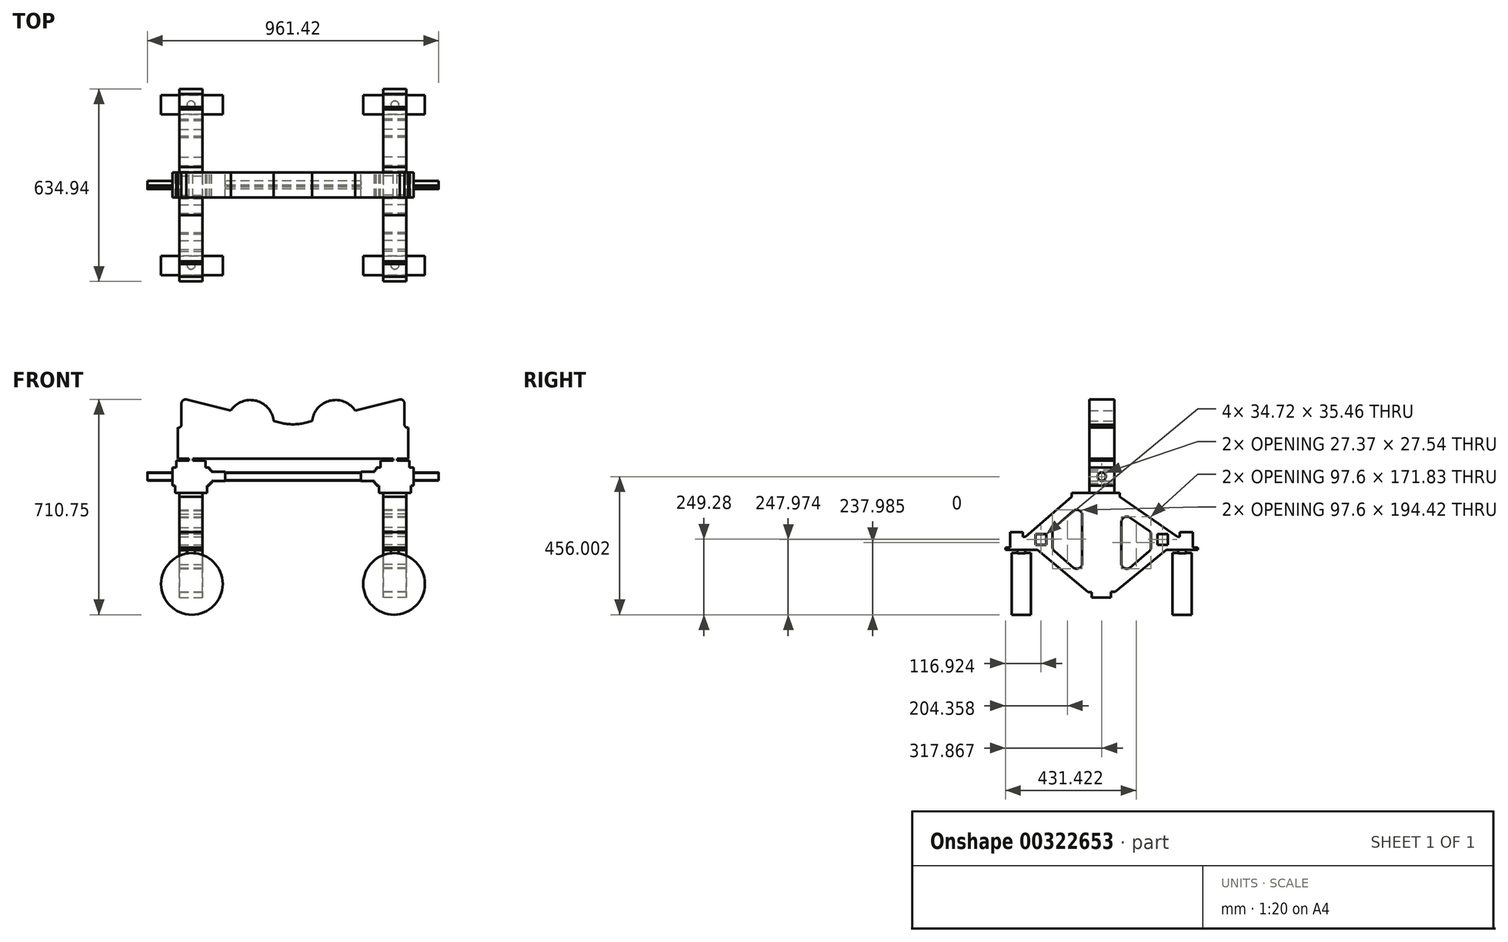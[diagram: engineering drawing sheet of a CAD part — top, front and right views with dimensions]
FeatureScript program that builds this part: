
annotation { "Feature Type Name" : "Feature", "Feature Type Description" : "" }
export const myFeature = defineFeature(function(context is Context, id is Id, definition is map)
    precondition{}
    {
        {
            var Q0;
            Q0=qCreatedBy(makeId("Front.planeOp"),FACE);
            var sketch = newSketch(context, id + "F0", { "sketchPlane" : qUnion([Q0])});
            skLineSegment(sketch, "E0", {"start": v(0, 0) * mm, "end": v(-380.7, 0) * mm});
            skLineSegment(sketch, "E1", {"start": v(-380.7, 0) * mm, "end": v(-380.7, 102.32) * mm});
            skArc(sketch, "E2", {"start": v(-380.7, 102.32) * mm, "mid": v(-372.54, 104.11) * mm, "end": v(-368.21, 111.26) * mm});
            skLineSegment(sketch, "E3", {"start": v(-368.21, 111.26) * mm, "end": v(-368.21, 182.25) * mm});
            skArc(sketch, "E4", {"start": v(-352.72, 195.3) * mm, "mid": v(-363.5, 192.37) * mm, "end": v(-368.21, 182.25) * mm});
            skLineSegment(sketch, "E5", {"start": v(-352.72, 195.3) * mm, "end": v(-38.9, 118.02) * mm});
            skLineSegment(sketch, "E6", {"start": v(0, 0) * mm, "end": v(0, 0) * mm});
            skArc(sketch, "E7.MirrorCS", {"start": v(380.7, 102.32) * mm, "mid": v(372.54, 104.11) * mm, "end": v(368.21, 111.26) * mm});
            skLineSegment(sketch, "E8.MirrorCS", {"start": v(368.21, 111.26) * mm, "end": v(368.21, 182.25) * mm});
            skArc(sketch, "E9.MirrorCS", {"start": v(352.72, 195.3) * mm, "mid": v(363.5, 192.37) * mm, "end": v(368.21, 182.25) * mm});
            skLineSegment(sketch, "E10.MirrorCS", {"start": v(0, 0) * mm, "end": v(380.7, 0) * mm});
            skLineSegment(sketch, "E11.MirrorCS", {"start": v(380.7, 0) * mm, "end": v(380.7, 102.32) * mm});
            skLineSegment(sketch, "E12.MirrorCS", {"start": v(352.72, 195.3) * mm, "end": v(38.9, 118.02) * mm});
            skArc(sketch, "E13", {"start": v(-38.9, 118.02) * mm, "mid": v(0, 113.3) * mm, "end": v(38.9, 118.02) * mm});
            skLineSegment(sketch, "E14", {"start": v(224.33, -43.67) * mm, "end": v(269.45, -43.67) * mm});
            skLineSegment(sketch, "E15", {"start": v(269.45, -43.67) * mm, "end": v(269.45, -36.61) * mm});
            skLineSegment(sketch, "E16", {"start": v(269.45, -36.61) * mm, "end": v(275.59, -36.61) * mm});
            skLineSegment(sketch, "E17", {"start": v(275.59, -36.61) * mm, "end": v(275.59, -29.55) * mm});
            skLineSegment(sketch, "E18", {"start": v(275.59, -29.55) * mm, "end": v(288.48, -29.55) * mm});
            skLineSegment(sketch, "E19", {"start": v(288.48, -29.55) * mm, "end": v(288.48, -5.92) * mm});
            skLineSegment(sketch, "E20", {"start": v(288.48, -5.92) * mm, "end": v(330.53, -5.92) * mm});
            skLineSegment(sketch, "E21", {"start": v(330.53, -5.92) * mm, "end": v(330.53, 0) * mm});
            skLineSegment(sketch, "E22", {"start": v(330.53, 0) * mm, "end": v(343.42, 0) * mm});
            skLineSegment(sketch, "E23", {"start": v(343.42, 0) * mm, "end": v(343.42, -5.92) * mm});
            skLineSegment(sketch, "E24", {"start": v(343.42, -5.92) * mm, "end": v(384.86, -5.92) * mm});
            skLineSegment(sketch, "E25", {"start": v(384.86, -5.92) * mm, "end": v(384.86, -29.55) * mm});
            skLineSegment(sketch, "E26", {"start": v(384.86, -29.55) * mm, "end": v(397.75, -29.55) * mm});
            skLineSegment(sketch, "E27", {"start": v(397.75, -29.55) * mm, "end": v(397.75, -88.49) * mm});
            skLineSegment(sketch, "E28", {"start": v(397.75, -88.49) * mm, "end": v(388.85, -88.49) * mm});
            skLineSegment(sketch, "E29", {"start": v(388.85, -88.49) * mm, "end": v(388.85, -112.74) * mm});
            skLineSegment(sketch, "E30", {"start": v(388.85, -112.74) * mm, "end": v(283.57, -112.74) * mm});
            skLineSegment(sketch, "E31", {"start": v(283.57, -112.74) * mm, "end": v(283.57, -88.49) * mm});
            skLineSegment(sketch, "E32", {"start": v(283.57, -88.49) * mm, "end": v(275.59, -88.49) * mm});
            skLineSegment(sketch, "E33", {"start": v(275.59, -88.49) * mm, "end": v(275.59, -80.81) * mm});
            skLineSegment(sketch, "E34", {"start": v(275.59, -80.81) * mm, "end": v(268.53, -80.81) * mm});
            skLineSegment(sketch, "E35", {"start": v(268.53, -80.81) * mm, "end": v(268.53, -73.14) * mm});
            skLineSegment(sketch, "E36", {"start": v(268.53, -73.14) * mm, "end": v(224.33, -73.14) * mm});
            skLineSegment(sketch, "E37", {"start": v(224.33, -73.14) * mm, "end": v(224.33, -43.67) * mm});
            skLineSegment(sketch, "E38", {"start": v(0, -43.67) * mm, "end": v(0, -73.14) * mm, "construction": true});
            skLineSegment(sketch, "E39.MirrorCS", {"start": v(-343.42, 0) * mm, "end": v(-343.42, -5.92) * mm});
            skLineSegment(sketch, "E40.MirrorCS", {"start": v(-283.57, -88.49) * mm, "end": v(-275.59, -88.49) * mm});
            skLineSegment(sketch, "E41.MirrorCS", {"start": v(-269.45, -43.67) * mm, "end": v(-269.45, -36.61) * mm});
            skLineSegment(sketch, "E42.MirrorCS", {"start": v(-275.59, -36.61) * mm, "end": v(-275.59, -29.55) * mm});
            skLineSegment(sketch, "E43.MirrorCS", {"start": v(-268.53, -80.81) * mm, "end": v(-268.53, -73.14) * mm});
            skLineSegment(sketch, "E44.MirrorCS", {"start": v(-397.75, -88.49) * mm, "end": v(-388.85, -88.49) * mm});
            skLineSegment(sketch, "E45.MirrorCS", {"start": v(-384.86, -29.55) * mm, "end": v(-397.75, -29.55) * mm});
            skLineSegment(sketch, "E46.MirrorCS", {"start": v(-275.59, -88.49) * mm, "end": v(-275.59, -80.81) * mm});
            skLineSegment(sketch, "E47.MirrorCS", {"start": v(-275.59, -29.55) * mm, "end": v(-288.48, -29.55) * mm});
            skLineSegment(sketch, "E48.MirrorCS", {"start": v(-330.53, -5.92) * mm, "end": v(-330.53, 0) * mm});
            skLineSegment(sketch, "E49.MirrorCS", {"start": v(-330.53, 0) * mm, "end": v(-343.42, 0) * mm});
            skLineSegment(sketch, "E50.MirrorCS", {"start": v(-275.59, -80.81) * mm, "end": v(-268.53, -80.81) * mm});
            skLineSegment(sketch, "E51.MirrorCS", {"start": v(-269.45, -36.61) * mm, "end": v(-275.59, -36.61) * mm});
            skLineSegment(sketch, "E52.MirrorCS", {"start": v(-283.57, -112.74) * mm, "end": v(-283.57, -88.49) * mm});
            skLineSegment(sketch, "E53.MirrorCS", {"start": v(-343.42, -5.92) * mm, "end": v(-384.86, -5.92) * mm});
            skLineSegment(sketch, "E54.MirrorCS", {"start": v(-288.48, -5.92) * mm, "end": v(-330.53, -5.92) * mm});
            skLineSegment(sketch, "E55.MirrorCS", {"start": v(-268.53, -73.14) * mm, "end": v(-224.33, -73.14) * mm});
            skLineSegment(sketch, "E56.MirrorCS", {"start": v(-288.48, -29.55) * mm, "end": v(-288.48, -5.92) * mm});
            skLineSegment(sketch, "E57.MirrorCS", {"start": v(-224.33, -73.14) * mm, "end": v(-224.33, -43.67) * mm});
            skLineSegment(sketch, "E58.MirrorCS", {"start": v(-388.85, -88.49) * mm, "end": v(-388.85, -112.74) * mm});
            skLineSegment(sketch, "E59.MirrorCS", {"start": v(-384.86, -5.92) * mm, "end": v(-384.86, -29.55) * mm});
            skLineSegment(sketch, "E60.MirrorCS", {"start": v(-388.85, -112.74) * mm, "end": v(-283.57, -112.74) * mm});
            skLineSegment(sketch, "E61.MirrorCS", {"start": v(-397.75, -29.55) * mm, "end": v(-397.75, -88.49) * mm});
            skLineSegment(sketch, "E62.MirrorCS", {"start": v(-224.33, -43.67) * mm, "end": v(-269.45, -43.67) * mm});
            skCircle(sketch, "E63", {"center": v(-140.68, 116.12) * mm, "radius": 77.5 * mm});
            skCircle(sketch, "E64", {"center": v(139.08, 116.12) * mm, "radius": 76.01 * mm});
            skLineSegment(sketch, "E65.bottom", {"start": v(-474.97, -45.5) * mm, "end": v(480.7, -45.5) * mm});
            skLineSegment(sketch, "E65.top", {"start": v(-474.97, -73.04) * mm, "end": v(480.7, -73.04) * mm});
            skLineSegment(sketch, "E65.left", {"start": v(-474.97, -45.5) * mm, "end": v(-474.97, -73.04) * mm});
            skLineSegment(sketch, "E65.right", {"start": v(480.7, -45.5) * mm, "end": v(480.7, -73.04) * mm});
            skSolve(sketch);
        }
        {
            var Q0;
            Q0=makeQuery(id+"F0.imprint","IMPRINT",FACE,{"disambiguationData":[TD([[makeQuery(id+"F0.imprint","IMPRINT",EDGE,{"derivedFrom":sQuery(id+"F0.wireOp",EDGE,"E2")}),-1.0]])]});
            var Q1;
            {var subQ0=sQuery(id+"F0.wireOp",EDGE,"E63");var subQ1=sQuery(id+"F0.wireOp",EDGE,"E5");var subQ2=makeQuery(id+"F0.imprint","INTERSECT",VERTEX,{"disambiguationData":[OD(0.0)],"derivedFrom":[subQ1,subQ0]});Q1=makeQuery(id+"F0.imprint","IMPRINT",FACE,{"disambiguationData":[TD([[makeQuery(id+"F0.imprint","IMPRINT",EDGE,{"disambiguationData":[TD([[subQ2,-1.0]])],"derivedFrom":subQ1}),-1.0]])]});}
            var Q2;
            {var subQ0=sQuery(id+"F0.wireOp",EDGE,"E64");var subQ1=sQuery(id+"F0.wireOp",EDGE,"E12.MirrorCS");var subQ2=makeQuery(id+"F0.imprint","INTERSECT",VERTEX,{"disambiguationData":[OD(0.0)],"derivedFrom":[subQ1,subQ0]});Q2=makeQuery(id+"F0.imprint","IMPRINT",FACE,{"disambiguationData":[TD([[makeQuery(id+"F0.imprint","IMPRINT",EDGE,{"disambiguationData":[TD([[subQ2,-1.0]])],"derivedFrom":subQ1}),1.0]])]});}
            var Q3;
            {var subQ0=sQuery(id+"F0.wireOp",EDGE,"E64");var subQ1=sQuery(id+"F0.wireOp",EDGE,"E12.MirrorCS");var subQ2=makeQuery(id+"F0.imprint","INTERSECT",VERTEX,{"disambiguationData":[OD(0.0)],"derivedFrom":[subQ1,subQ0]});Q3=makeQuery(id+"F0.imprint","IMPRINT",FACE,{"disambiguationData":[TD([[makeQuery(id+"F0.imprint","IMPRINT",EDGE,{"disambiguationData":[TD([[subQ2,-1.0]])],"derivedFrom":subQ1}),-1.0]])]});}
            var Q4;
            {var subQ0=sQuery(id+"F0.wireOp",EDGE,"E63");var subQ1=sQuery(id+"F0.wireOp",EDGE,"E5");var subQ2=makeQuery(id+"F0.imprint","INTERSECT",VERTEX,{"disambiguationData":[OD(0.0)],"derivedFrom":[subQ1,subQ0]});Q4=makeQuery(id+"F0.imprint","IMPRINT",FACE,{"disambiguationData":[TD([[makeQuery(id+"F0.imprint","IMPRINT",EDGE,{"disambiguationData":[TD([[subQ2,-1.0]])],"derivedFrom":subQ1}),1.0]])]});}
            var Q5;
            {var subQ2=sQuery(id+"F0.wireOp",EDGE,"E14");Q5=makeQuery(id+"F0.imprint","IMPRINT",FACE,{"disambiguationData":[TD([[makeQuery(id+"F0.imprint","IMPRINT",EDGE,{"derivedFrom":subQ2}),-1.0]])]});}
            var Q6;
            {var subQ0=sQuery(id+"F0.wireOp",EDGE,"E65.bottom");var subQ1=sQuery(id+"F0.wireOp",EDGE,"E27");var subQ2=makeQuery(id+"F0.imprint","INTERSECT",VERTEX,{"derivedFrom":[subQ1,subQ0]});Q6=makeQuery(id+"F0.imprint","IMPRINT",FACE,{"disambiguationData":[TD([[makeQuery(id+"F0.imprint","IMPRINT",EDGE,{"disambiguationData":[TD([[subQ2,-1.0]])],"derivedFrom":subQ1}),-1.0]])]});}
            var Q7;
            {var subQ1=sQuery(id+"F0.wireOp",EDGE,"E28");Q7=makeQuery(id+"F0.imprint","IMPRINT",FACE,{"disambiguationData":[TD([[makeQuery(id+"F0.imprint","IMPRINT",EDGE,{"derivedFrom":subQ1}),-1.0]])]});}
            var Q8;
            {var subQ0=sQuery(id+"F0.wireOp",EDGE,"E65.top");var subQ1=sQuery(id+"F0.wireOp",EDGE,"E57.MirrorCS");var subQ2=makeQuery(id+"F0.imprint","INTERSECT",VERTEX,{"derivedFrom":[subQ1,subQ0]});Q8=makeQuery(id+"F0.imprint","IMPRINT",FACE,{"disambiguationData":[TD([[makeQuery(id+"F0.imprint","IMPRINT",EDGE,{"disambiguationData":[TD([[subQ2,-1.0]])],"derivedFrom":subQ1}),1.0]])]});}
            var Q9;
            {var subQ6=sQuery(id+"F0.wireOp",EDGE,"E39.MirrorCS");Q9=makeQuery(id+"F0.imprint","IMPRINT",FACE,{"disambiguationData":[TD([[makeQuery(id+"F0.imprint","IMPRINT",EDGE,{"derivedFrom":subQ6}),1.0]])]});}
            var Q10;
            Q10=makeQuery(id+"F0.imprint","IMPRINT",FACE,{"disambiguationData":[TD([[makeQuery(id+"F0.imprint","IMPRINT",EDGE,{"derivedFrom":sQuery(id+"F0.wireOp",EDGE,"E40.MirrorCS")}),1.0]])]});
            extrude(context, id + "F1", {"entities" : qUnion([Q0, Q1, Q2, Q3, Q4, Q5, Q6, Q7, Q8, Q9, Q10]), "endBound" : BoundingType.SYMMETRIC, "depth" : 82.55 * mm});
        }
        {
            var Q0;
            Q0=makeQuery(id+"F1.opExtrude","SWEPT_FACE",FACE,{"disambiguationData":[OSD([sQuery(id+"F0.wireOp",EDGE,"E61.MirrorCS")])]});
            var sketch = newSketch(context, id + "F2", { "sketchPlane" : qUnion([Q0])});
            skCircle(sketch, "E66", {"center": v(0, -59.02) * mm, "radius": 13.7 * mm});
            skPoint(sketch, "E66.centerSnap0", {"position": v(0, -29.55) * mm});
            skPoint(sketch, "E66.centerSnap1", {"position": v(41.28, -59.02) * mm});
            skSolve(sketch);
        }
        {
            var Q0;
            {var subQ5=sQuery(id+"F0.wireOp",EDGE,"E65.left");Q0=makeQuery(id+"F0.imprint","IMPRINT",FACE,{"disambiguationData":[TD([[makeQuery(id+"F0.imprint","IMPRINT",EDGE,{"derivedFrom":subQ5}),1.0]])]});}
            extrude(context, id + "F3", {"entities" : qUnion([Q0]), "operationType" : NewBodyOperationType.ADD, "depth" : 6.35 * mm});
        }
        {
            var Q0;
            Q0=makeQuery(id+"F2.imprint","IMPRINT",FACE,{"disambiguationData":[TD([[makeQuery(id+"F2.imprint","IMPRINT",EDGE,{"derivedFrom":sQuery(id+"F2.wireOp",EDGE,"E66")}),1.0]])]});
            var Q1;
            Q1=makeQuery(id+"F3.opExtrude","SWEPT_FACE",FACE,{"disambiguationData":[OSD([sQuery(id+"F0.wireOp",EDGE,"E65.left")])]});
            extrude(context, id + "F4", {"entities" : qUnion([Q0]), "operationType" : NewBodyOperationType.ADD, "endBound" : BoundingType.UP_TO_SURFACE, "endBoundEntityFace" : qUnion([Q1]), "depth" : 25.4 * mm});
        }
        {
            var Q0;
            Q0=qCreatedBy(makeId("Right.planeOp"),FACE);
            var sketch = newSketch(context, id + "F5", { "sketchPlane" : qUnion([Q0])});
            skLineSegment(sketch, "E67", {"start": v(0, -571.18) * mm, "end": v(-32.87, -571.18) * mm});
            skLineSegment(sketch, "E68", {"start": v(-32.87, -571.18) * mm, "end": v(-32.87, -553.22) * mm});
            skLineSegment(sketch, "E69", {"start": v(-32.87, -553.22) * mm, "end": v(-45.24, -553.22) * mm});
            skLineSegment(sketch, "E70", {"start": v(-45.24, -553.22) * mm, "end": v(-212.9, -413.1) * mm});
            skLineSegment(sketch, "E71", {"start": v(-212.9, -413.1) * mm, "end": v(-317.9, -413.1) * mm});
            skLineSegment(sketch, "E72", {"start": v(-317.9, -413.1) * mm, "end": v(-317.9, -405.92) * mm});
            skLineSegment(sketch, "E73", {"start": v(-317.9, -405.92) * mm, "end": v(-302.72, -405.92) * mm});
            skLineSegment(sketch, "E74", {"start": v(-302.72, -405.92) * mm, "end": v(-302.72, -355.62) * mm});
            skLineSegment(sketch, "E75", {"start": v(-302.72, -355.62) * mm, "end": v(-260.8, -355.62) * mm});
            skLineSegment(sketch, "E76", {"start": v(-260.8, -355.62) * mm, "end": v(-260.8, -370.39) * mm});
            skLineSegment(sketch, "E77", {"start": v(-260.8, -370.39) * mm, "end": v(-251.63, -370.39) * mm});
            skLineSegment(sketch, "E78", {"start": v(-251.63, -370.39) * mm, "end": v(-99.11, -238.64) * mm});
            skLineSegment(sketch, "E79", {"start": v(-99.11, -238.64) * mm, "end": v(-99.11, -225.32) * mm});
            skLineSegment(sketch, "E80", {"start": v(-99.11, -225.32) * mm, "end": v(59.68, -225.32) * mm});
            skLineSegment(sketch, "E81", {"start": v(59.68, -225.32) * mm, "end": v(59.68, -238.64) * mm});
            skLineSegment(sketch, "E82", {"start": v(59.68, -238.64) * mm, "end": v(249.9, -370.39) * mm});
            skLineSegment(sketch, "E83", {"start": v(249.9, -370.39) * mm, "end": v(257.9, -370.39) * mm});
            skLineSegment(sketch, "E84", {"start": v(257.9, -370.39) * mm, "end": v(257.9, -355.34) * mm});
            skLineSegment(sketch, "E85", {"start": v(257.9, -355.34) * mm, "end": v(300.53, -355.34) * mm});
            skLineSegment(sketch, "E86", {"start": v(300.53, -355.34) * mm, "end": v(300.53, -405.92) * mm});
            skLineSegment(sketch, "E87", {"start": v(300.53, -405.92) * mm, "end": v(317.05, -405.92) * mm});
            skLineSegment(sketch, "E88", {"start": v(317.05, -405.92) * mm, "end": v(317.05, -413.1) * mm});
            skLineSegment(sketch, "E89", {"start": v(317.05, -413.1) * mm, "end": v(213.14, -413.1) * mm});
            skLineSegment(sketch, "E90", {"start": v(213.14, -413.1) * mm, "end": v(44.76, -552.5) * mm});
            skLineSegment(sketch, "E91", {"start": v(44.76, -552.5) * mm, "end": v(30.37, -552.5) * mm});
            skLineSegment(sketch, "E92", {"start": v(30.37, -552.5) * mm, "end": v(30.37, -571.18) * mm});
            skLineSegment(sketch, "E93", {"start": v(30.37, -571.18) * mm, "end": v(0, -571.18) * mm});
            skLineSegment(sketch, "E94.bottom", {"start": v(-218.32, -362.15) * mm, "end": v(-183.6, -362.15) * mm});
            skLineSegment(sketch, "E94.top", {"start": v(-218.32, -397.61) * mm, "end": v(-183.6, -397.61) * mm});
            skLineSegment(sketch, "E94.left", {"start": v(-218.32, -362.15) * mm, "end": v(-218.32, -397.61) * mm});
            skLineSegment(sketch, "E94.right", {"start": v(-183.6, -362.15) * mm, "end": v(-183.6, -397.61) * mm});
            skLineSegment(sketch, "E95", {"start": v(-162.33, -378.58) * mm, "end": v(-162.33, -351.33) * mm});
            skArc(sketch, "E96", {"start": v(-156.73, -339.38) * mm, "mid": v(-160.86, -344.73) * mm, "end": v(-162.33, -351.33) * mm});
            skLineSegment(sketch, "E97", {"start": v(-156.73, -339.38) * mm, "end": v(-92.67, -284.02) * mm});
            skArc(sketch, "E98", {"start": v(-64.73, -295.08) * mm, "mid": v(-75.96, -282.63) * mm, "end": v(-92.67, -284.02) * mm});
            skLineSegment(sketch, "E99", {"start": v(-64.73, -295.08) * mm, "end": v(-64.73, -378.58) * mm});
            skLineSegment(sketch, "E100.MirrorCS", {"start": v(-162.33, -378.58) * mm, "end": v(-162.33, -405.82) * mm});
            skArc(sketch, "E101.MirrorCS", {"start": v(-156.73, -417.77) * mm, "mid": v(-160.86, -412.42) * mm, "end": v(-162.33, -405.82) * mm});
            skLineSegment(sketch, "E102.MirrorCS", {"start": v(-156.73, -417.77) * mm, "end": v(-92.67, -473.14) * mm});
            skArc(sketch, "E103.MirrorCS", {"start": v(-64.73, -462.07) * mm, "mid": v(-75.96, -474.52) * mm, "end": v(-92.67, -473.14) * mm});
            skLineSegment(sketch, "E104.MirrorCS", {"start": v(-64.73, -462.07) * mm, "end": v(-64.73, -378.58) * mm});
            skArc(sketch, "E105.MirrorCS", {"start": v(156.73, -417.77) * mm, "mid": v(160.86, -412.42) * mm, "end": v(162.33, -405.82) * mm});
            skLineSegment(sketch, "E106.MirrorCS", {"start": v(156.73, -417.77) * mm, "end": v(92.67, -473.14) * mm});
            skArc(sketch, "E107.MirrorCS", {"start": v(64.73, -462.07) * mm, "mid": v(75.96, -474.52) * mm, "end": v(92.67, -473.14) * mm});
            skLineSegment(sketch, "E108.MirrorCS", {"start": v(218.32, -362.15) * mm, "end": v(183.6, -362.15) * mm});
            skLineSegment(sketch, "E109.MirrorCS", {"start": v(218.32, -362.15) * mm, "end": v(218.32, -397.61) * mm});
            skLineSegment(sketch, "E110.MirrorCS", {"start": v(218.32, -397.61) * mm, "end": v(183.6, -397.61) * mm});
            skLineSegment(sketch, "E111.MirrorCS", {"start": v(183.6, -362.15) * mm, "end": v(183.6, -397.61) * mm});
            skLineSegment(sketch, "E112", {"start": v(64.73, -462.07) * mm, "end": v(64.73, -321.96) * mm});
            skArc(sketch, "E113", {"start": v(91.9, -306.46) * mm, "mid": v(73.82, -306.32) * mm, "end": v(64.73, -321.96) * mm});
            skLineSegment(sketch, "E114", {"start": v(91.9, -306.46) * mm, "end": v(156.74, -351.56) * mm});
            skLineSegment(sketch, "E115", {"start": v(162.33, -405.82) * mm, "end": v(162.33, -360.74) * mm});
            skArc(sketch, "E116", {"start": v(162.33, -360.74) * mm, "mid": v(160.82, -355.36) * mm, "end": v(156.74, -351.56) * mm});
            skSolve(sketch);
        }
        {
            var Q0;
            Q0=makeQuery(id+"F5.imprint","IMPRINT",FACE,{"disambiguationData":[TD([[makeQuery(id+"F5.imprint","IMPRINT",EDGE,{"derivedFrom":sQuery(id+"F5.wireOp",EDGE,"E67")}),-1.0]])]});
            extrude(context, id + "F6", {"entities" : qUnion([Q0]), "depth" : 76.2 * mm});
        }
        {
            var Q0;
            Q0=makeQuery(id+"F6.opExtrude","SWEPT_BODY",BODY,{"disambiguationData":[OSD([sQuery(id+"F5.wireOp",EDGE,"E67"),sQuery(id+"F5.wireOp",EDGE,"E68"),sQuery(id+"F5.wireOp",EDGE,"E69"),sQuery(id+"F5.wireOp",EDGE,"E70"),sQuery(id+"F5.wireOp",EDGE,"E71"),sQuery(id+"F5.wireOp",EDGE,"E72"),sQuery(id+"F5.wireOp",EDGE,"E73"),sQuery(id+"F5.wireOp",EDGE,"E74"),sQuery(id+"F5.wireOp",EDGE,"E75"),sQuery(id+"F5.wireOp",EDGE,"E76"),sQuery(id+"F5.wireOp",EDGE,"E77"),sQuery(id+"F5.wireOp",EDGE,"E78"),sQuery(id+"F5.wireOp",EDGE,"E79"),sQuery(id+"F5.wireOp",EDGE,"E80"),sQuery(id+"F5.wireOp",EDGE,"E81"),sQuery(id+"F5.wireOp",EDGE,"E82"),sQuery(id+"F5.wireOp",EDGE,"E83"),sQuery(id+"F5.wireOp",EDGE,"E84"),sQuery(id+"F5.wireOp",EDGE,"E85"),sQuery(id+"F5.wireOp",EDGE,"E86"),sQuery(id+"F5.wireOp",EDGE,"E87"),sQuery(id+"F5.wireOp",EDGE,"E88"),sQuery(id+"F5.wireOp",EDGE,"E89"),sQuery(id+"F5.wireOp",EDGE,"E90"),sQuery(id+"F5.wireOp",EDGE,"E91"),sQuery(id+"F5.wireOp",EDGE,"E92"),sQuery(id+"F5.wireOp",EDGE,"E93"),sQuery(id+"F5.wireOp",EDGE,"E94.bottom"),sQuery(id+"F5.wireOp",EDGE,"E94.top"),sQuery(id+"F5.wireOp",EDGE,"E94.left"),sQuery(id+"F5.wireOp",EDGE,"E94.right"),sQuery(id+"F5.wireOp",EDGE,"E95"),sQuery(id+"F5.wireOp",EDGE,"E96"),sQuery(id+"F5.wireOp",EDGE,"E97"),sQuery(id+"F5.wireOp",EDGE,"E98"),sQuery(id+"F5.wireOp",EDGE,"E99"),sQuery(id+"F5.wireOp",EDGE,"E100.MirrorCS"),sQuery(id+"F5.wireOp",EDGE,"E101.MirrorCS"),sQuery(id+"F5.wireOp",EDGE,"E102.MirrorCS"),sQuery(id+"F5.wireOp",EDGE,"E103.MirrorCS"),sQuery(id+"F5.wireOp",EDGE,"E104.MirrorCS"),sQuery(id+"F5.wireOp",EDGE,"E105.MirrorCS"),sQuery(id+"F5.wireOp",EDGE,"E106.MirrorCS"),sQuery(id+"F5.wireOp",EDGE,"E107.MirrorCS"),sQuery(id+"F5.wireOp",EDGE,"E108.MirrorCS"),sQuery(id+"F5.wireOp",EDGE,"E109.MirrorCS"),sQuery(id+"F5.wireOp",EDGE,"E110.MirrorCS"),sQuery(id+"F5.wireOp",EDGE,"E111.MirrorCS"),sQuery(id+"F5.wireOp",EDGE,"E112"),sQuery(id+"F5.wireOp",EDGE,"E113"),sQuery(id+"F5.wireOp",EDGE,"E114"),sQuery(id+"F5.wireOp",EDGE,"E115"),sQuery(id+"F5.wireOp",EDGE,"E116")])]});
            var Q1;
            Q1=sQuery(id+"F0.wireOp",EDGE,"E10.MirrorCS");
            var Q2;
            Q2=sQuery(id+"F0.wireOp",EDGE,"E10.MirrorCS");
            transform(context, id + "F7", {"entities" : qUnion([Q0]), "transformType" : TransformType.TRANSLATION_DISTANCE, "transformDirection" : qUnion([Q2]), "distance" : 298.45 * mm, "makeCopy" : false});
        }
        {
            var Q0;
            Q0=makeQuery(id+"F6.opExtrude","SWEPT_BODY",BODY,{"disambiguationData":[OSD([sQuery(id+"F5.wireOp",EDGE,"E67"),sQuery(id+"F5.wireOp",EDGE,"E68"),sQuery(id+"F5.wireOp",EDGE,"E69"),sQuery(id+"F5.wireOp",EDGE,"E70"),sQuery(id+"F5.wireOp",EDGE,"E71"),sQuery(id+"F5.wireOp",EDGE,"E72"),sQuery(id+"F5.wireOp",EDGE,"E73"),sQuery(id+"F5.wireOp",EDGE,"E74"),sQuery(id+"F5.wireOp",EDGE,"E75"),sQuery(id+"F5.wireOp",EDGE,"E76"),sQuery(id+"F5.wireOp",EDGE,"E77"),sQuery(id+"F5.wireOp",EDGE,"E78"),sQuery(id+"F5.wireOp",EDGE,"E79"),sQuery(id+"F5.wireOp",EDGE,"E80"),sQuery(id+"F5.wireOp",EDGE,"E81"),sQuery(id+"F5.wireOp",EDGE,"E82"),sQuery(id+"F5.wireOp",EDGE,"E83"),sQuery(id+"F5.wireOp",EDGE,"E84"),sQuery(id+"F5.wireOp",EDGE,"E85"),sQuery(id+"F5.wireOp",EDGE,"E86"),sQuery(id+"F5.wireOp",EDGE,"E87"),sQuery(id+"F5.wireOp",EDGE,"E88"),sQuery(id+"F5.wireOp",EDGE,"E89"),sQuery(id+"F5.wireOp",EDGE,"E90"),sQuery(id+"F5.wireOp",EDGE,"E91"),sQuery(id+"F5.wireOp",EDGE,"E92"),sQuery(id+"F5.wireOp",EDGE,"E93"),sQuery(id+"F5.wireOp",EDGE,"E94.bottom"),sQuery(id+"F5.wireOp",EDGE,"E94.top"),sQuery(id+"F5.wireOp",EDGE,"E94.left"),sQuery(id+"F5.wireOp",EDGE,"E94.right"),sQuery(id+"F5.wireOp",EDGE,"E95"),sQuery(id+"F5.wireOp",EDGE,"E96"),sQuery(id+"F5.wireOp",EDGE,"E97"),sQuery(id+"F5.wireOp",EDGE,"E98"),sQuery(id+"F5.wireOp",EDGE,"E99"),sQuery(id+"F5.wireOp",EDGE,"E100.MirrorCS"),sQuery(id+"F5.wireOp",EDGE,"E101.MirrorCS"),sQuery(id+"F5.wireOp",EDGE,"E102.MirrorCS"),sQuery(id+"F5.wireOp",EDGE,"E103.MirrorCS"),sQuery(id+"F5.wireOp",EDGE,"E104.MirrorCS"),sQuery(id+"F5.wireOp",EDGE,"E105.MirrorCS"),sQuery(id+"F5.wireOp",EDGE,"E106.MirrorCS"),sQuery(id+"F5.wireOp",EDGE,"E107.MirrorCS"),sQuery(id+"F5.wireOp",EDGE,"E108.MirrorCS"),sQuery(id+"F5.wireOp",EDGE,"E109.MirrorCS"),sQuery(id+"F5.wireOp",EDGE,"E110.MirrorCS"),sQuery(id+"F5.wireOp",EDGE,"E111.MirrorCS"),sQuery(id+"F5.wireOp",EDGE,"E112"),sQuery(id+"F5.wireOp",EDGE,"E113"),sQuery(id+"F5.wireOp",EDGE,"E114"),sQuery(id+"F5.wireOp",EDGE,"E115"),sQuery(id+"F5.wireOp",EDGE,"E116")])]});
            var Q1;
            Q1=makeQuery(id+"F1.opExtrude","CAP_EDGE",EDGE,{"disambiguationData":[OSD([sQuery(id+"F0.wireOp",EDGE,"E11.MirrorCS")])],"isStart":true});
            transform(context, id + "F8", {"entities" : qUnion([Q0]), "transformType" : TransformType.TRANSLATION_DISTANCE, "transformDirection" : qUnion([Q1]), "distance" : 112.6 * mm, "makeCopy" : false});
        }
        {
            var Q0;
            Q0=makeQuery(id+"F6.opExtrude","SWEPT_BODY",BODY,{"disambiguationData":[OSD([sQuery(id+"F5.wireOp",EDGE,"E67"),sQuery(id+"F5.wireOp",EDGE,"E68"),sQuery(id+"F5.wireOp",EDGE,"E69"),sQuery(id+"F5.wireOp",EDGE,"E70"),sQuery(id+"F5.wireOp",EDGE,"E71"),sQuery(id+"F5.wireOp",EDGE,"E72"),sQuery(id+"F5.wireOp",EDGE,"E73"),sQuery(id+"F5.wireOp",EDGE,"E74"),sQuery(id+"F5.wireOp",EDGE,"E75"),sQuery(id+"F5.wireOp",EDGE,"E76"),sQuery(id+"F5.wireOp",EDGE,"E77"),sQuery(id+"F5.wireOp",EDGE,"E78"),sQuery(id+"F5.wireOp",EDGE,"E79"),sQuery(id+"F5.wireOp",EDGE,"E80"),sQuery(id+"F5.wireOp",EDGE,"E81"),sQuery(id+"F5.wireOp",EDGE,"E82"),sQuery(id+"F5.wireOp",EDGE,"E83"),sQuery(id+"F5.wireOp",EDGE,"E84"),sQuery(id+"F5.wireOp",EDGE,"E85"),sQuery(id+"F5.wireOp",EDGE,"E86"),sQuery(id+"F5.wireOp",EDGE,"E87"),sQuery(id+"F5.wireOp",EDGE,"E88"),sQuery(id+"F5.wireOp",EDGE,"E89"),sQuery(id+"F5.wireOp",EDGE,"E90"),sQuery(id+"F5.wireOp",EDGE,"E91"),sQuery(id+"F5.wireOp",EDGE,"E92"),sQuery(id+"F5.wireOp",EDGE,"E93"),sQuery(id+"F5.wireOp",EDGE,"E94.bottom"),sQuery(id+"F5.wireOp",EDGE,"E94.top"),sQuery(id+"F5.wireOp",EDGE,"E94.left"),sQuery(id+"F5.wireOp",EDGE,"E94.right"),sQuery(id+"F5.wireOp",EDGE,"E95"),sQuery(id+"F5.wireOp",EDGE,"E96"),sQuery(id+"F5.wireOp",EDGE,"E97"),sQuery(id+"F5.wireOp",EDGE,"E98"),sQuery(id+"F5.wireOp",EDGE,"E99"),sQuery(id+"F5.wireOp",EDGE,"E100.MirrorCS"),sQuery(id+"F5.wireOp",EDGE,"E101.MirrorCS"),sQuery(id+"F5.wireOp",EDGE,"E102.MirrorCS"),sQuery(id+"F5.wireOp",EDGE,"E103.MirrorCS"),sQuery(id+"F5.wireOp",EDGE,"E104.MirrorCS"),sQuery(id+"F5.wireOp",EDGE,"E105.MirrorCS"),sQuery(id+"F5.wireOp",EDGE,"E106.MirrorCS"),sQuery(id+"F5.wireOp",EDGE,"E107.MirrorCS"),sQuery(id+"F5.wireOp",EDGE,"E108.MirrorCS"),sQuery(id+"F5.wireOp",EDGE,"E109.MirrorCS"),sQuery(id+"F5.wireOp",EDGE,"E110.MirrorCS"),sQuery(id+"F5.wireOp",EDGE,"E111.MirrorCS"),sQuery(id+"F5.wireOp",EDGE,"E112"),sQuery(id+"F5.wireOp",EDGE,"E113"),sQuery(id+"F5.wireOp",EDGE,"E114"),sQuery(id+"F5.wireOp",EDGE,"E115"),sQuery(id+"F5.wireOp",EDGE,"E116")])]});
            var Q1;
            Q1=qCreatedBy(makeId("Right.planeOp"),FACE);
            mirror(context, id + "F9", {"operationType" : NewBodyOperationType.ADD, "entities" : qUnion([Q0]), "mirrorPlane" : qUnion([Q1])});
        }
        {
            var Q0;
            {var subQ0=sQuery(id+"F0.wireOp",EDGE,"E65.left");Q0=makeQuery(id+"F4.boolean.opBoolean","MERGE",FACE,{"derivedFrom":[makeQuery(id+"F3.opExtrude","SWEPT_FACE",FACE,{"disambiguationData":[OSD([subQ0])]}),makeQuery(id+"F4.opExtrude","CAP_FACE",FACE,{"disambiguationData":[OSD([subQ0])],"isStart":false})]});}
            extrude(context, id + "F10", {"entities" : qUnion([Q0]), "operationType" : NewBodyOperationType.ADD, "oppositeDirection" : true, "depth" : 955.67 * mm});
        }
        {
            var Q0;
            Q0=makeQuery(id+"F9.opPattern","COPY",FACE,{"derivedFrom":makeQuery(id+"F6.opExtrude","SWEPT_FACE",FACE,{"disambiguationData":[OSD([sQuery(id+"F5.wireOp",EDGE,"E89")])]}),"instanceName":"1"});
            var sketch = newSketch(context, id + "F11", { "sketchPlane" : qUnion([Q0])});
            skCircle(sketch, "E117", {"center": v(336.55, 265.4) * mm, "radius": 12.7 * mm});
            skPoint(sketch, "E117.centerSnap0", {"position": v(374.65, 265.4) * mm});
            skPoint(sketch, "E117.centerSnap1", {"position": v(336.55, 317.9) * mm});
            skCircle(sketch, "E118", {"center": v(-336.55, 265.4) * mm, "radius": 12.7 * mm});
            skPoint(sketch, "E118.centerSnap0", {"position": v(-336.55, 317.9) * mm});
            skPoint(sketch, "E118.centerSnap1", {"position": v(-298.45, 265.4) * mm});
            skCircle(sketch, "E119", {"center": v(-336.55, -265.1) * mm, "radius": 12.7 * mm});
            skPoint(sketch, "E119.centerSnap0", {"position": v(-336.55, -317.05) * mm});
            skPoint(sketch, "E119.centerSnap1", {"position": v(-374.65, -265.1) * mm});
            skCircle(sketch, "E120", {"center": v(336.55, -265.1) * mm, "radius": 12.7 * mm});
            skSolve(sketch);
        }
        {
            var Q0;
            Q0=makeQuery(id+"F11.imprint","IMPRINT",FACE,{"disambiguationData":[TD([[makeQuery(id+"F11.imprint","IMPRINT",EDGE,{"derivedFrom":sQuery(id+"F11.wireOp",EDGE,"E117")}),1.0]])]});
            var Q1;
            Q1=makeQuery(id+"F11.imprint","IMPRINT",FACE,{"disambiguationData":[TD([[makeQuery(id+"F11.imprint","IMPRINT",EDGE,{"derivedFrom":sQuery(id+"F11.wireOp",EDGE,"E119")}),1.0]])]});
            var Q2;
            Q2=makeQuery(id+"F11.imprint","IMPRINT",FACE,{"disambiguationData":[TD([[makeQuery(id+"F11.imprint","IMPRINT",EDGE,{"derivedFrom":sQuery(id+"F11.wireOp",EDGE,"E120")}),1.0]])]});
            var Q3;
            Q3=makeQuery(id+"F11.imprint","IMPRINT",FACE,{"disambiguationData":[TD([[makeQuery(id+"F11.imprint","IMPRINT",EDGE,{"derivedFrom":sQuery(id+"F11.wireOp",EDGE,"E118")}),1.0]])]});
            extrude(context, id + "F12", {"entities" : qUnion([Q0, Q1, Q2, Q3]), "operationType" : NewBodyOperationType.ADD, "depth" : 127 * mm});
        }
        {
            var Q0;
            Q0=makeQuery(id+"F6.opExtrude","SWEPT_FACE",FACE,{"disambiguationData":[OSD([sQuery(id+"F5.wireOp",EDGE,"E86")])]});
            var sketch = newSketch(context, id + "F13", { "sketchPlane" : qUnion([Q0])});
            skCircle(sketch, "E121", {"center": v(-390.92, -413.53) * mm, "radius": 101.74 * mm});
            skSolve(sketch);
        }
        {
            var Q0;
            Q0 = qSketchRegion(id + "F13", true);
            extrude(context, id + "F14", {"entities" : qUnion([Q0]), "operationType" : NewBodyOperationType.ADD, "depth" : 63.5 * mm});
        }
        {
            var Q0;
            Q0=makeQuery(id+"F14.opExtrude","SWEPT_BODY",BODY,{"disambiguationData":[OSD([sQuery(id+"F13.wireOp",EDGE,"E121")])]});
            var Q1;
            Q1=makeQuery(id+"F6.opExtrude","CAP_EDGE",EDGE,{"disambiguationData":[OSD([sQuery(id+"F5.wireOp",EDGE,"E89")])],"isStart":true});
            transform(context, id + "F15", {"entities" : qUnion([Q0]), "transformType" : TransformType.TRANSLATION_DISTANCE, "transformDirection" : qUnion([Q1]), "distance" : 66.67 * mm, "makeCopy" : false});
        }
        {
            var Q0;
            Q0=makeQuery(id+"F14.opExtrude","SWEPT_BODY",BODY,{"disambiguationData":[OSD([sQuery(id+"F13.wireOp",EDGE,"E121")])]});
            var Q1;
            Q1=makeQuery(id+"F6.opExtrude","SWEPT_EDGE",EDGE,{"disambiguationData":[OSD([sQuery(id+"F5.wireOp",EDGE,"E88"),sQuery(id+"F5.wireOp",EDGE,"E89")])]});
            transform(context, id + "F16", {"entities" : qUnion([Q0]), "transformType" : TransformType.TRANSLATION_DISTANCE, "transformDirection" : qUnion([Q1]), "distance" : 57.15 * mm, "makeCopy" : false});
        }
        {
            var Q0;
            Q0=makeQuery(id+"F14.opExtrude","SWEPT_BODY",BODY,{"disambiguationData":[OSD([sQuery(id+"F13.wireOp",EDGE,"E121")])]});
            var Q1;
            Q1=qCreatedBy(makeId("Front.planeOp"),FACE);
            mirror(context, id + "F17", {"operationType" : NewBodyOperationType.ADD, "entities" : qUnion([Q0]), "mirrorPlane" : qUnion([Q1])});
        }
        {
            var Q0;
            Q0=makeQuery(id+"F1.opExtrude","SWEPT_BODY",BODY,{"disambiguationData":[OSD([sQuery(id+"F0.wireOp",EDGE,"E2"),sQuery(id+"F0.wireOp",EDGE,"E3"),sQuery(id+"F0.wireOp",EDGE,"E4"),sQuery(id+"F0.wireOp",EDGE,"E5"),sQuery(id+"F0.wireOp",EDGE,"E7.MirrorCS"),sQuery(id+"F0.wireOp",EDGE,"E8.MirrorCS"),sQuery(id+"F0.wireOp",EDGE,"E9.MirrorCS"),sQuery(id+"F0.wireOp",EDGE,"E11.MirrorCS"),sQuery(id+"F0.wireOp",EDGE,"E12.MirrorCS"),sQuery(id+"F0.wireOp",EDGE,"E13"),sQuery(id+"F0.wireOp",EDGE,"E14"),sQuery(id+"F0.wireOp",EDGE,"E15"),sQuery(id+"F0.wireOp",EDGE,"E16"),sQuery(id+"F0.wireOp",EDGE,"E17"),sQuery(id+"F0.wireOp",EDGE,"E18"),sQuery(id+"F0.wireOp",EDGE,"E19"),sQuery(id+"F0.wireOp",EDGE,"E20"),sQuery(id+"F0.wireOp",EDGE,"E21"),sQuery(id+"F0.wireOp",EDGE,"E23"),sQuery(id+"F0.wireOp",EDGE,"E24"),sQuery(id+"F0.wireOp",EDGE,"E25"),sQuery(id+"F0.wireOp",EDGE,"E26"),sQuery(id+"F0.wireOp",EDGE,"E27"),sQuery(id+"F0.wireOp",EDGE,"E28"),sQuery(id+"F0.wireOp",EDGE,"E29"),sQuery(id+"F0.wireOp",EDGE,"E30"),sQuery(id+"F0.wireOp",EDGE,"E31"),sQuery(id+"F0.wireOp",EDGE,"E32"),sQuery(id+"F0.wireOp",EDGE,"E33"),sQuery(id+"F0.wireOp",EDGE,"E34"),sQuery(id+"F0.wireOp",EDGE,"E35"),sQuery(id+"F0.wireOp",EDGE,"E36"),sQuery(id+"F0.wireOp",EDGE,"E37"),sQuery(id+"F0.wireOp",EDGE,"E39.MirrorCS"),sQuery(id+"F0.wireOp",EDGE,"E40.MirrorCS"),sQuery(id+"F0.wireOp",EDGE,"E41.MirrorCS"),sQuery(id+"F0.wireOp",EDGE,"E42.MirrorCS"),sQuery(id+"F0.wireOp",EDGE,"E43.MirrorCS"),sQuery(id+"F0.wireOp",EDGE,"E44.MirrorCS"),sQuery(id+"F0.wireOp",EDGE,"E45.MirrorCS"),sQuery(id+"F0.wireOp",EDGE,"E46.MirrorCS"),sQuery(id+"F0.wireOp",EDGE,"E47.MirrorCS"),sQuery(id+"F0.wireOp",EDGE,"E48.MirrorCS"),sQuery(id+"F0.wireOp",EDGE,"E50.MirrorCS"),sQuery(id+"F0.wireOp",EDGE,"E51.MirrorCS"),sQuery(id+"F0.wireOp",EDGE,"E52.MirrorCS"),sQuery(id+"F0.wireOp",EDGE,"E0"),sQuery(id+"F0.wireOp",EDGE,"E53.MirrorCS"),sQuery(id+"F0.wireOp",EDGE,"E54.MirrorCS"),sQuery(id+"F0.wireOp",EDGE,"E55.MirrorCS"),sQuery(id+"F0.wireOp",EDGE,"E1"),sQuery(id+"F0.wireOp",EDGE,"E56.MirrorCS"),sQuery(id+"F0.wireOp",EDGE,"E57.MirrorCS"),sQuery(id+"F0.wireOp",EDGE,"E58.MirrorCS"),sQuery(id+"F0.wireOp",EDGE,"E59.MirrorCS"),sQuery(id+"F0.wireOp",EDGE,"E60.MirrorCS"),sQuery(id+"F0.wireOp",EDGE,"E61.MirrorCS"),sQuery(id+"F0.wireOp",EDGE,"E62.MirrorCS"),sQuery(id+"F0.wireOp",EDGE,"E10.MirrorCS"),sQuery(id+"F0.wireOp",EDGE,"E63"),sQuery(id+"F0.wireOp",EDGE,"E64")])]});
            var Q1;
            Q1=qCreatedBy(makeId("Right.planeOp"),FACE);
            mirror(context, id + "F18", {"operationType" : NewBodyOperationType.ADD, "entities" : qUnion([Q0]), "mirrorPlane" : qUnion([Q1])});
        }
    });
